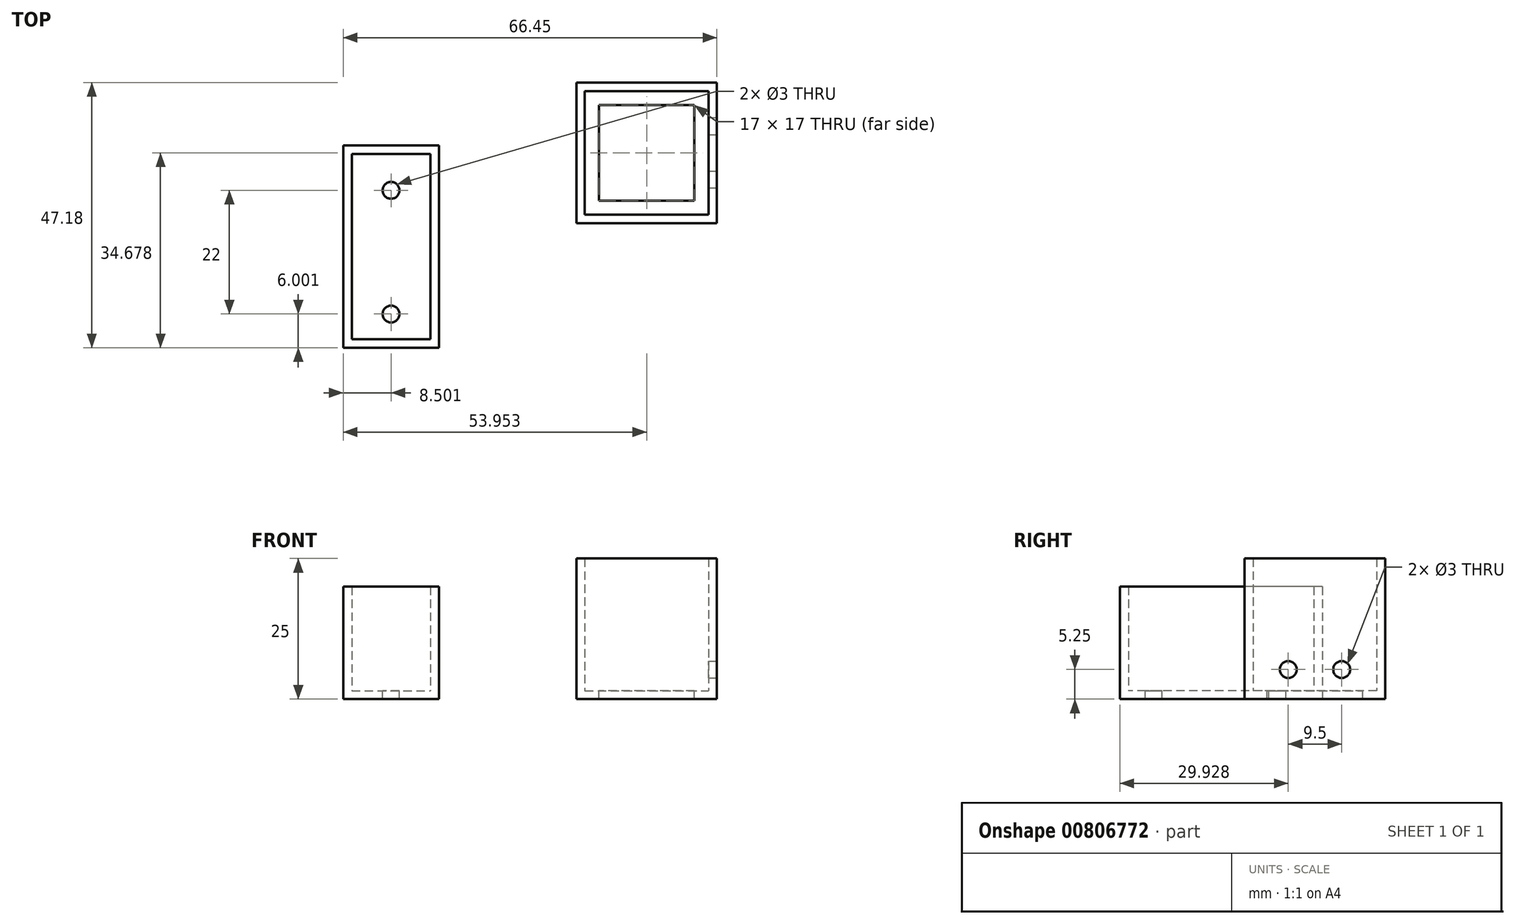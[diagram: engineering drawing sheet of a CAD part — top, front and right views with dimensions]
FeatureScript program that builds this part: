
annotation { "Feature Type Name" : "Feature", "Feature Type Description" : "" }
export const myFeature = defineFeature(function(context is Context, id is Id, definition is map)
    precondition{}
    {
        {
            var Q0;
            Q0=qCreatedBy(makeId("Top.planeOp"),FACE);
            var sketch = newSketch(context, id + "F0", { "sketchPlane" : qUnion([Q0])});
            skLineSegment(sketch, "E0.bottom", {"start": v(-36.82, 44.12) * mm, "end": v(-19.82, 44.12) * mm});
            skLineSegment(sketch, "E0.top", {"start": v(-36.82, 8.12) * mm, "end": v(-19.82, 8.12) * mm});
            skLineSegment(sketch, "E0.left", {"start": v(-36.82, 44.12) * mm, "end": v(-36.82, 8.12) * mm});
            skLineSegment(sketch, "E0.right", {"start": v(-19.82, 44.12) * mm, "end": v(-19.82, 8.12) * mm});
            skSolve(sketch);
        }
        {
            var Q0;
            Q0 = qSketchRegion(id + "F0", true);
            extrude(context, id + "F1", {"entities" : qUnion([Q0]), "depth" : 20 * mm, "offsetDistance" : 25 * mm});
        }
        {
            var Q0;
            Q0=makeQuery(id+"F1.opExtrude","CAP_FACE",FACE,{"disambiguationData":[OSD([sQuery(id+"F0.wireOp",EDGE,"E0.bottom"),sQuery(id+"F0.wireOp",EDGE,"E0.top"),sQuery(id+"F0.wireOp",EDGE,"E0.left"),sQuery(id+"F0.wireOp",EDGE,"E0.right")])],"isStart":false});
            shell(context, id + "F2", {"entities" : qUnion([Q0]), "thickness" : 1.5 * mm});
        }
        {
            var Q0;
            Q0=qCreatedBy(makeId("Top.planeOp"),FACE);
            var sketch = newSketch(context, id + "F3", { "sketchPlane" : qUnion([Q0])});
            skLineSegment(sketch, "E1.bottom", {"start": v(4.63, 55.3) * mm, "end": v(29.63, 55.3) * mm});
            skLineSegment(sketch, "E1.top", {"start": v(4.63, 30.3) * mm, "end": v(29.63, 30.3) * mm});
            skLineSegment(sketch, "E1.left", {"start": v(4.63, 55.3) * mm, "end": v(4.63, 30.3) * mm});
            skLineSegment(sketch, "E1.right", {"start": v(29.63, 55.3) * mm, "end": v(29.63, 30.3) * mm});
            skSolve(sketch);
        }
        {
            var Q0;
            Q0=makeQuery(id+"F3.imprint","IMPRINT",FACE,{"disambiguationData":[TD([[makeQuery(id+"F3.imprint","IMPRINT",EDGE,{"derivedFrom":sQuery(id+"F3.wireOp",EDGE,"E1.bottom")}),-1.0]])]});
            extrude(context, id + "F4", {"entities" : qUnion([Q0]), "depth" : 25 * mm, "offsetDistance" : 25 * mm});
        }
        {
            var Q0;
            Q0=makeQuery(id+"F4.opExtrude","CAP_FACE",FACE,{"disambiguationData":[OSD([sQuery(id+"F3.wireOp",EDGE,"E1.bottom"),sQuery(id+"F3.wireOp",EDGE,"E1.top"),sQuery(id+"F3.wireOp",EDGE,"E1.left"),sQuery(id+"F3.wireOp",EDGE,"E1.right")])],"isStart":false});
            shell(context, id + "F5", {"entities" : qUnion([Q0]), "thickness" : 1.5 * mm});
        }
        {
            var Q0;
            Q0=makeQuery(id+"F4.opExtrude","SWEPT_FACE",FACE,{"disambiguationData":[OSD([sQuery(id+"F3.wireOp",EDGE,"E1.right")])]});
            var sketch = newSketch(context, id + "F6", { "sketchPlane" : qUnion([Q0])});
            skCircle(sketch, "E2", {"center": v(38.05, 5.25) * mm, "radius": 1.5 * mm});
            skCircle(sketch, "E3", {"center": v(47.55, 5.25) * mm, "radius": 1.5 * mm});
            skSolve(sketch);
        }
        {
            var Q0;
            Q0=makeQuery(id+"F5.opShell","OFFSET_FACE",FACE,{"disambiguationData":[OSD([sQuery(id+"F3.wireOp",EDGE,"E1.bottom"),sQuery(id+"F3.wireOp",EDGE,"E1.top"),sQuery(id+"F3.wireOp",EDGE,"E1.left"),sQuery(id+"F3.wireOp",EDGE,"E1.right")])]});
            var sketch = newSketch(context, id + "F7", { "sketchPlane" : qUnion([Q0])});
            skLineSegment(sketch, "E4.bottom", {"start": v(25.63, 34.3) * mm, "end": v(8.63, 34.3) * mm});
            skLineSegment(sketch, "E4.top", {"start": v(25.63, 51.3) * mm, "end": v(8.63, 51.3) * mm});
            skLineSegment(sketch, "E4.left", {"start": v(25.63, 34.3) * mm, "end": v(25.63, 51.3) * mm});
            skLineSegment(sketch, "E4.right", {"start": v(8.63, 34.3) * mm, "end": v(8.63, 51.3) * mm});
            skSolve(sketch);
        }
        {
            var Q0;
            Q0 = qSketchRegion(id + "F7", true);
            extrude(context, id + "F8", {"entities" : qUnion([Q0]), "operationType" : NewBodyOperationType.REMOVE, "oppositeDirection" : true, "depth" : 25 * mm, "offsetDistance" : 25 * mm});
        }
        {
            var Q0;
            Q0=makeQuery(id+"F2.opShell","OFFSET_FACE",FACE,{"disambiguationData":[OSD([sQuery(id+"F0.wireOp",EDGE,"E0.bottom"),sQuery(id+"F0.wireOp",EDGE,"E0.top"),sQuery(id+"F0.wireOp",EDGE,"E0.left"),sQuery(id+"F0.wireOp",EDGE,"E0.right")])]});
            var sketch = newSketch(context, id + "F9", { "sketchPlane" : qUnion([Q0])});
            skCircle(sketch, "E5", {"center": v(-28.32, 36.12) * mm, "radius": 1.5 * mm});
            skPoint(sketch, "E5.centerSnap0", {"position": v(-28.32, 42.62) * mm});
            skCircle(sketch, "E6", {"center": v(-28.32, 14.12) * mm, "radius": 1.5 * mm});
            skSolve(sketch);
        }
        {
            var Q0;
            Q0 = qSketchRegion(id + "F9", true);
            extrude(context, id + "F10", {"entities" : qUnion([Q0]), "operationType" : NewBodyOperationType.REMOVE, "oppositeDirection" : true, "depth" : 63.5 * mm, "offsetDistance" : 25 * mm});
        }
        {
            var Q0;
            Q0 = qSketchRegion(id + "F6", true);
            extrude(context, id + "F11", {"entities" : qUnion([Q0]), "operationType" : NewBodyOperationType.REMOVE, "oppositeDirection" : true, "depth" : 10 * mm, "offsetDistance" : 25 * mm});
        }
    });
